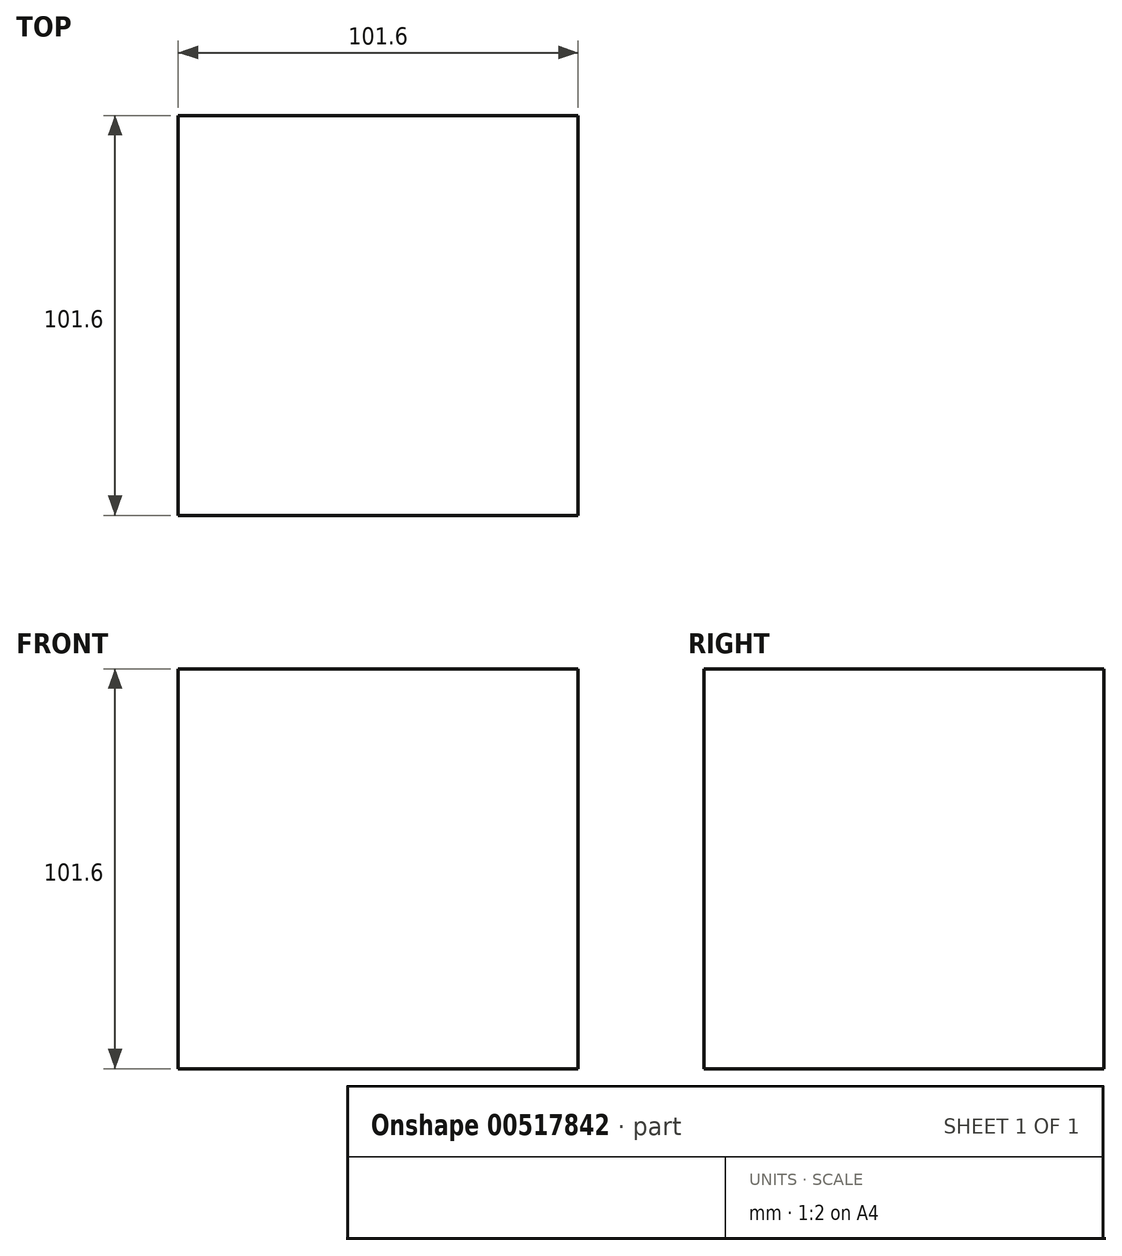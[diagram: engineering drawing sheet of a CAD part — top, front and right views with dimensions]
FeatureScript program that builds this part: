
annotation { "Feature Type Name" : "Feature", "Feature Type Description" : "" }
export const myFeature = defineFeature(function(context is Context, id is Id, definition is map)
    precondition{}
    {
        {
            var Q0;
            Q0=qCreatedBy(makeId("Top.planeOp"),FACE);
            var sketch = newSketch(context, id + "F0", { "sketchPlane" : qUnion([Q0])});
            skLineSegment(sketch, "E0.bottom", {"start": v(-53.54, 63.43) * mm, "end": v(48.06, 63.43) * mm});
            skLineSegment(sketch, "E0.top", {"start": v(-53.54, -38.17) * mm, "end": v(48.06, -38.17) * mm});
            skLineSegment(sketch, "E0.left", {"start": v(-53.54, 63.43) * mm, "end": v(-53.54, -38.17) * mm});
            skLineSegment(sketch, "E0.right", {"start": v(48.06, 63.43) * mm, "end": v(48.06, -38.17) * mm});
            skSolve(sketch);
        }
        {
            var Q0;
            Q0 = qSketchRegion(id + "F0", true);
            extrude(context, id + "F1", {"entities" : qUnion([Q0]), "depth" : 101.6 * mm, "offsetDistance" : 25.4 * mm});
        }
    });
